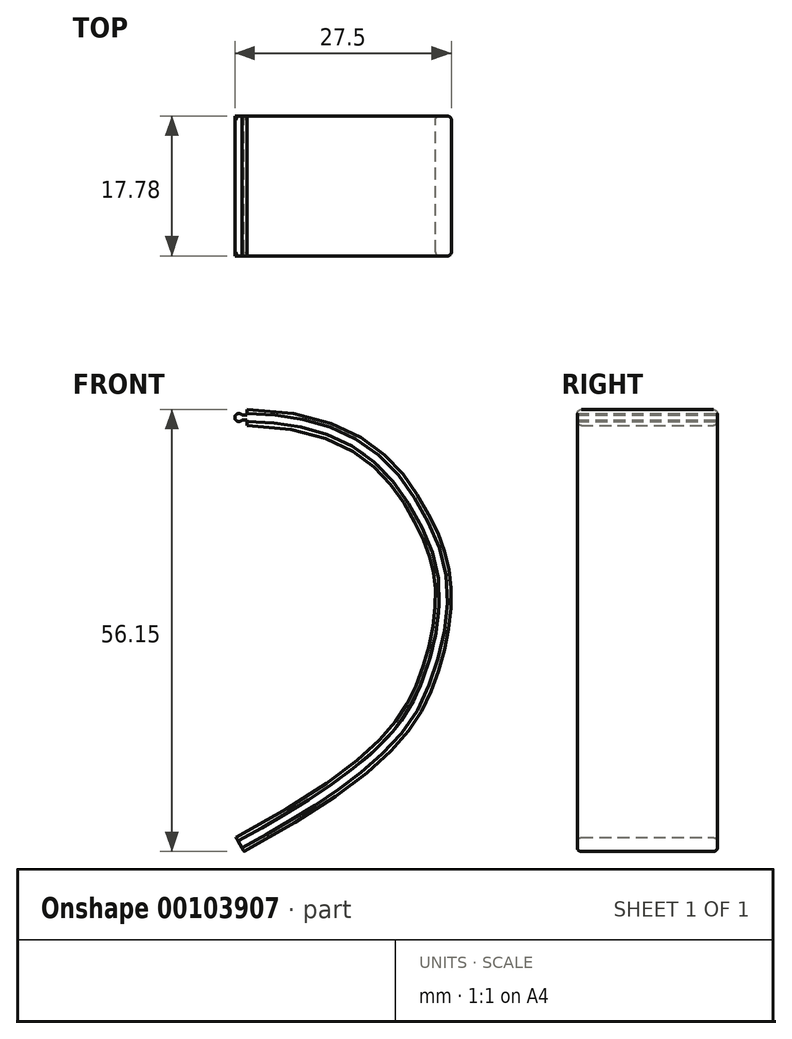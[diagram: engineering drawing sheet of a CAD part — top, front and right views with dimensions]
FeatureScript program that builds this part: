
annotation { "Feature Type Name" : "Feature", "Feature Type Description" : "" }
export const myFeature = defineFeature(function(context is Context, id is Id, definition is map)
    precondition{}
    {
        {
            var Q0;
            Q0=qCreatedBy(makeId("Front.planeOp"),FACE);
            var sketch = newSketch(context, id + "F0", { "sketchPlane" : qUnion([Q0])});
            skFitSpline(sketch, "E0", {"points": [v(0, 33.71) * mm, v(23.32, 20.8) * mm, v(26.69, 10.41) * mm, v(24.48, -2.04) * mm, v(0, -23.82) * mm], "startDerivative": vector(152.5, -2.09) * mm, "endDerivative": vector(-166.41, -90.8) * mm});
            skSolve(sketch);
        }
        {
            var Q0;
            Q0=qCreatedBy(makeId("Right.planeOp"),FACE);
            var sketch = newSketch(context, id + "F1", { "sketchPlane" : qUnion([Q0])});
            skLineSegment(sketch, "E1.bottom", {"start": v(-9.1, 32.98) * mm, "end": v(8.68, 32.98) * mm});
            skLineSegment(sketch, "E1.top", {"start": v(-9.1, 30.94) * mm, "end": v(8.68, 30.94) * mm});
            skLineSegment(sketch, "E1.left", {"start": v(-9.1, 32.98) * mm, "end": v(-9.1, 30.94) * mm});
            skLineSegment(sketch, "E1.right", {"start": v(8.68, 32.98) * mm, "end": v(8.68, 30.94) * mm});
            skSolve(sketch);
        }
        {
            var Q0;
            Q0=makeQuery(id+"F1.imprint","IMPRINT",FACE,{"disambiguationData":[TD([[makeQuery(id+"F1.imprint","IMPRINT",EDGE,{"derivedFrom":sQuery(id+"F1.wireOp",EDGE,"E1.bottom")}),-1.0]])]});
            var Q1;
            Q1=sQuery(id+"F0.wireOp",EDGE,"E0");
            sweep(context, id + "F2", {"profiles" : qUnion([Q0]), "path" : qUnion([Q1])});
        }
        {
            var Q0;
            Q0=makeQuery(id+"F2.opSweep","SWEPT_FACE",FACE,{"disambiguationData":[OSD([sQuery(id+"F0.wireOp",EDGE,"d5144ba9-9f09-4d0d-81a9-fa149cf3e8d82"),sQuery(id+"F1.wireOp",EDGE,"E1.right")])]});
            var sketch = newSketch(context, id + "F3", { "sketchPlane" : qUnion([Q0])});
            skCircle(sketch, "E2", {"center": v(1.02, 31.96) * mm, "radius": 0.5 * mm});
            skLineSegment(sketch, "E3", {"start": v(0.64, 32.3) * mm, "end": v(0, 32.3) * mm});
            skLineSegment(sketch, "E4", {"start": v(0.64, 31.62) * mm, "end": v(0, 31.62) * mm});
            skLineSegment(sketch, "E5", {"start": v(1.02, 31.96) * mm, "end": v(0, 31.96) * mm, "construction": true});
            skSolve(sketch);
        }
        {
            var Q0;
            {var subQ0=sQuery(id+"F3.wireOp",EDGE,"E3");Q0=makeQuery(id+"F3.imprint","IMPRINT",FACE,{"disambiguationData":[TD([[makeQuery(id+"F3.imprint","IMPRINT",EDGE,{"derivedFrom":subQ0}),1.0]])]});}
            var Q1;
            {var subQ0=sQuery(id+"F3.wireOp",EDGE,"E2");var subQ1=makeQuery(id+"F3.imprint","INTERSECT",VERTEX,{"derivedFrom":[subQ0,sQuery(id+"F3.wireOp",EDGE,"E3")]});Q1=makeQuery(id+"F3.imprint","IMPRINT",FACE,{"disambiguationData":[TD([[makeQuery(id+"F3.imprint","IMPRINT",EDGE,{"disambiguationData":[TD([[subQ1,-1.0]])],"derivedFrom":subQ0}),1.0]])]});}
            extrude(context, id + "F4", {"entities" : qUnion([Q0, Q1]), "operationType" : NewBodyOperationType.ADD, "oppositeDirection" : true, "depth" : 17.78 * mm});
        }
        {
            var Q0;
            Q0=makeQuery(id+"F2.opSweep","SWEPT_EDGE",EDGE,{"disambiguationData":[OSD([sQuery(id+"F0.wireOp",EDGE,"E0"),sQuery(id+"F1.wireOp",EDGE,"E1.bottom"),sQuery(id+"F1.wireOp",EDGE,"E1.right")])]});
            var Q1;
            Q1=makeQuery(id+"F2.opSweep","SWEPT_EDGE",EDGE,{"disambiguationData":[OSD([sQuery(id+"F0.wireOp",EDGE,"E0"),sQuery(id+"F1.wireOp",EDGE,"E1.top"),sQuery(id+"F1.wireOp",EDGE,"E1.right")])]});
            var Q2;
            Q2=makeQuery(id+"F2.opSweep","SWEPT_EDGE",EDGE,{"disambiguationData":[OSD([sQuery(id+"F0.wireOp",EDGE,"E0"),sQuery(id+"F1.wireOp",EDGE,"E1.bottom"),sQuery(id+"F1.wireOp",EDGE,"E1.left")])]});
            var Q3;
            Q3=makeQuery(id+"F2.opSweep","SWEPT_EDGE",EDGE,{"disambiguationData":[OSD([sQuery(id+"F0.wireOp",EDGE,"E0"),sQuery(id+"F1.wireOp",EDGE,"E1.top"),sQuery(id+"F1.wireOp",EDGE,"E1.left")])]});
            fillet(context, id + "F5", {"entities" : qUnion([Q0, Q1, Q2, Q3]), "radius" : 0.5 * mm, "tangentPropagation" : true, "allowEdgeOverflow" : false});
        }
    });
